# Revit family: Backwaren-Kühltische400x600 - Eigen
name_source: partatom
category: Sonderausstattung
revit_build: Autodesk Revit 2015 (Build: 20160512_1515(x64)
units: mm (PartAtom-declared; Revit-internal decimal feet)

## types (2) — shared parameters
Abstand Display seitlich = 60 mm  [stored 0.19685 ft]
Abstand Logo = 265 mm
Aufkantung Höhe = 50 mm  [stored 0.164042 ft]
Aufkantung Stärke = 6 mm  [stored 0.019685 ft]
Höhe Elektroanschluss = 150 mm
Korpus Höhe = 650 mm  [stored 2.13255 ft]
Korpus Tiefe = 720 mm
Kälteleistung = 380 Watt -15°C VT
Kältemittel = R134a
Material = Edelstahl AISI 304
Pfosten 1 = Ja
Pfosten Breite = 100 mm  [stored 0.328084 ft]
Pfosten Tiefe = 50 mm  [stored 0.164042 ft]
Platte Tiefe = 800 mm  [stored 2.62467 ft]
Pole = 1
Rückwand Stärke = 50 mm  [stored 0.164042 ft]
Scheinleistung = 0 VA
Seitenteil Breite = 320 mm  [stored 1.04987 ft]
Seitenteilwand Stärke = 15 mm  [stored 0.0492126 ft]
Seitenwand Stärke = 50 mm  [stored 0.164042 ft]
Sockelhöhe = 150 mm
Spannung = 230 V
Temp. Bereich = -2°C / +10°C
Tür_1 = Ja
Tür_2 = Ja
Türen Breite = 495 mm  [stored 1.62402 ft]
Türen Breite halb = 248 mm
Türen Höhe = 630 mm  [stored 2.06693 ft]
Türen Stärke = 50 mm  [stored 0.164042 ft]
Versatz Tür zu Seitenteil = 30 mm  [stored 0.0984252 ft]
Wand oben Stärke = 50 mm  [stored 0.164042 ft]
Wand unten Stärke = 50 mm  [stored 0.164042 ft]
Öffnungstiefe = 570 mm

## per-type parameters (varying)
| type | Artnr mit Platte | Artnr mit Platte und Aufkantung | Artnr ohne Platte | Breite | Energieverbrauch | Kapazität | Korpus Breite | Marmorplatte Material | Pfosten 2 | Pfosten Abstand | Pfosten Anzahl | Tür_3 | Türen Anzahl | Türen Lücke | Watt |
| 650x1400 2-türig | KTM 824662 | KTM 824661 | KTM 824660 | 1400 mm | 3,25 kWh / 24 h | 2 x 10 x EN6040 | 1065 mm | Marmor | Nein | 510 mm | 1 | Nein | 2 | 30 mm  [stored 0.0984252 ft] | 440 W |
| 650x1945 3-türig | KTM 834662 | KTM 834661 | KTM 834660 | 1945 mm  [stored 6.38123 ft] | 3,75 kWh / 24 h | 3 x 10 x EN6040 | 1610 mm | <Nach Kategorie> | Ja | 515 mm | 2 | Ja | 3 | 40 mm | 460 W |

note: [stored X ft] marks values corroborated as IEEE doubles in the binary element streams (Revit-internal decimal feet)

## geometry (parser evidence)
native form markers: Blend x13, Sweep x3
no freeform markers — native parametric forms only
